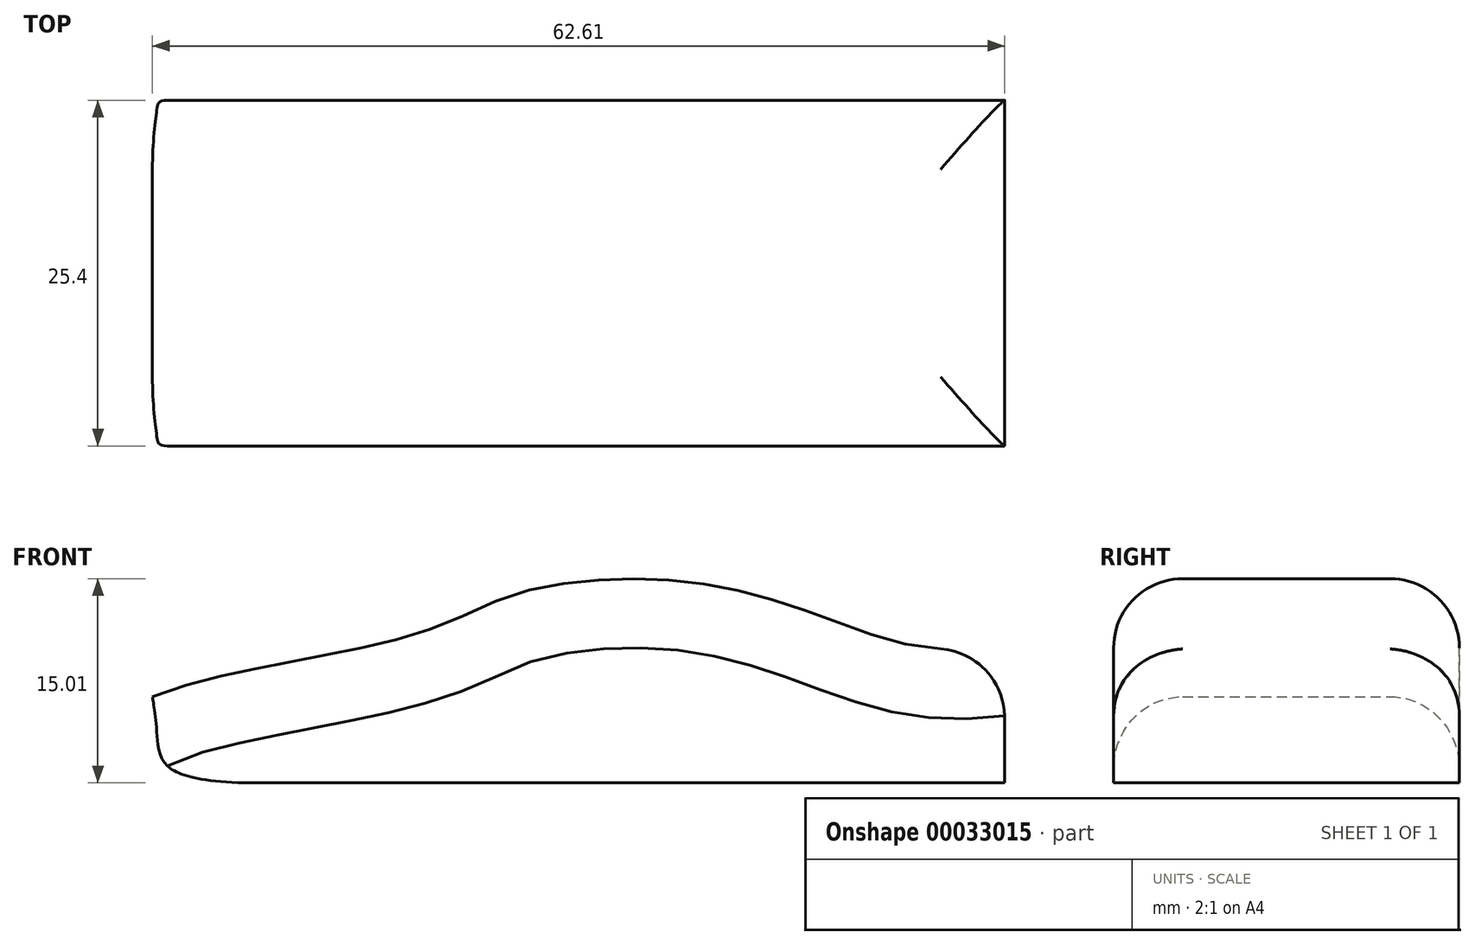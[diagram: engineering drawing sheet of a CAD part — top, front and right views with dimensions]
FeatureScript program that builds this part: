
annotation { "Feature Type Name" : "Feature", "Feature Type Description" : "" }
export const myFeature = defineFeature(function(context is Context, id is Id, definition is map)
    precondition{}
    {
        {
            var Q0;
            Q0=qCreatedBy(makeId("Front.planeOp"),FACE);
            var sketch = newSketch(context, id + "F0", { "sketchPlane" : qUnion([Q0])});
            skLineSegment(sketch, "E0", {"start": v(-20.51, 0) * mm, "end": v(34.28, 0) * mm});
            skLineSegment(sketch, "E1", {"start": v(34.28, 0) * mm, "end": v(34.28, 10.08) * mm});
            skFitSpline(sketch, "E2", {"points": [v(34.28, 10.08) * mm, v(21.63, 11.95) * mm, v(10.73, 14.81) * mm, v(-1.49, 13.93) * mm, v(-9.3, 10.85) * mm, v(-28.33, 6.33) * mm], "startDerivative": vector(-84.27, -13.41) * mm, "endDerivative": vector(-45.13, -21.01) * mm});
            skFitSpline(sketch, "E3", {"points": [v(-28.33, 6.33) * mm, v(-27.79, 2.16) * mm, v(-20.51, 0) * mm], "startDerivative": vector(3, -17.97) * mm, "endDerivative": vector(30.95, 0) * mm});
            skSolve(sketch);
        }
        {
            var Q0;
            Q0 = qSketchRegion(id + "F0", true);
            extrude(context, id + "F1", {"entities" : qUnion([Q0]), "depth" : 25.4 * mm});
        }
        {
            var Q0;
            Q0=makeQuery(id+"F1.opExtrude","CAP_EDGE",EDGE,{"disambiguationData":[OSD([sQuery(id+"F0.wireOp",EDGE,"E2")])],"isStart":true});
            var Q1;
            Q1=makeQuery(id+"F1.opExtrude","CAP_EDGE",EDGE,{"disambiguationData":[OSD([sQuery(id+"F0.wireOp",EDGE,"E2")])],"isStart":false});
            var Q2;
            Q2=makeQuery(id+"F1.opExtrude","SWEPT_EDGE",EDGE,{"disambiguationData":[OSD([sQuery(id+"F0.wireOp",EDGE,"E1"),sQuery(id+"F0.wireOp",EDGE,"E2")])]});
            fillet(context, id + "F2", {"entities" : qUnion([Q0, Q1, Q2]), "radius" : 5.08 * mm, "tangentPropagation" : true, "allowEdgeOverflow" : false});
        }
    });
